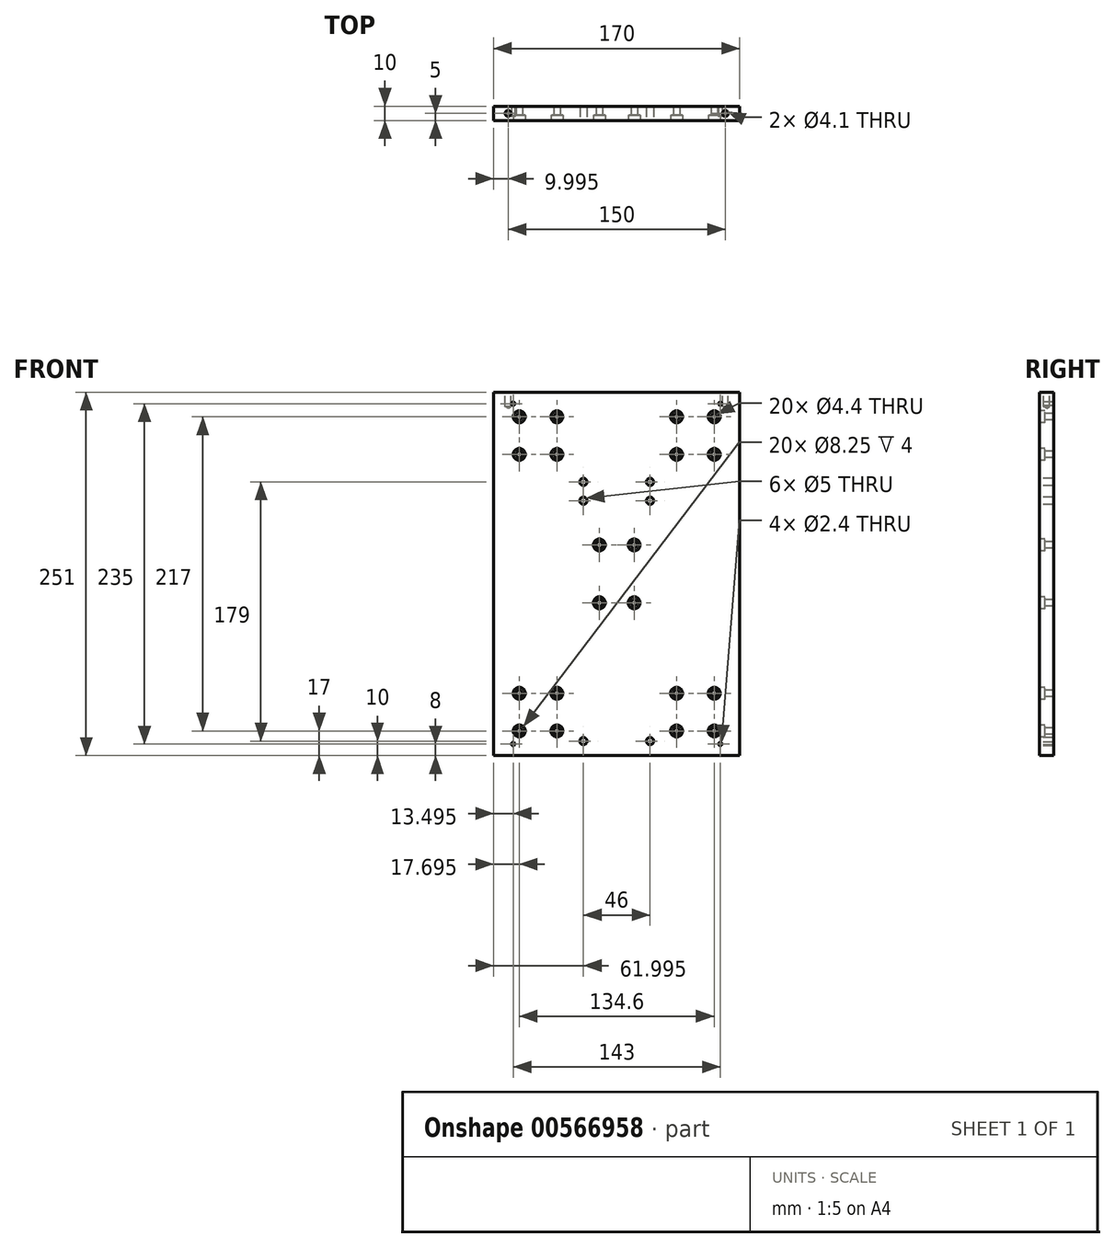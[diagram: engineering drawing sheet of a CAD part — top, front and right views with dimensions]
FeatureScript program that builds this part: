
annotation { "Feature Type Name" : "Feature", "Feature Type Description" : "" }
export const myFeature = defineFeature(function(context is Context, id is Id, definition is map)
    precondition{}
    {
        {
            var Q0;
            Q0=qCreatedBy(makeId("Front.planeOp"),FACE);
            var sketch = newSketch(context, id + "F0", { "sketchPlane" : qUnion([Q0])});
            skLineSegment(sketch, "E0.bottom", {"start": v(-43.58, 205.06) * mm, "end": v(126.42, 205.06) * mm});
            skLineSegment(sketch, "E0.top", {"start": v(-43.58, -40.94) * mm, "end": v(126.42, -40.94) * mm});
            skLineSegment(sketch, "E0.left", {"start": v(-43.58, 205.06) * mm, "end": v(-43.58, -40.94) * mm});
            skLineSegment(sketch, "E0.right", {"start": v(126.42, 205.06) * mm, "end": v(126.42, -40.94) * mm});
            skSolve(sketch);
        }
        {
            var Q0;
            Q0=makeQuery(id+"F0.imprint","IMPRINT",FACE,{"disambiguationData":[TD([[makeQuery(id+"F0.imprint","IMPRINT",EDGE,{"derivedFrom":sQuery(id+"F0.wireOp",EDGE,"E0.bottom")}),-1.0]])]});
            extrude(context, id + "F1", {"entities" : qUnion([Q0]), "depth" : 10 * mm});
        }
        {
            var Q0;
            Q0=makeQuery(id+"F1.opExtrude","CAP_FACE",FACE,{"disambiguationData":[OSD([sQuery(id+"F0.wireOp",EDGE,"E0.bottom"),sQuery(id+"F0.wireOp",EDGE,"E0.top"),sQuery(id+"F0.wireOp",EDGE,"E0.left"),sQuery(id+"F0.wireOp",EDGE,"E0.right")])],"isStart":false});
            var sketch = newSketch(context, id + "F2", { "sketchPlane" : qUnion([Q0])});
            skLineSegment(sketch, "E1", {"start": v(41.42, 205.06) * mm, "end": v(41.42, -40.94) * mm, "construction": true});
            skLineSegment(sketch, "E2", {"start": v(-30.08, 205.06) * mm, "end": v(-30.08, -40.94) * mm, "construction": true});
            skLineSegment(sketch, "E3.MirrorCS", {"start": v(112.92, 205.06) * mm, "end": v(112.92, -40.94) * mm, "construction": true});
            skLineSegment(sketch, "E4", {"start": v(112.92, 202.06) * mm, "end": v(-30.08, 202.06) * mm, "construction": true});
            skLineSegment(sketch, "E5", {"start": v(112.92, -32.94) * mm, "end": v(-30.08, -32.94) * mm, "construction": true});
            skPoint(sketch, "E6", {"position": v(112.92, 202.06) * mm});
            skPoint(sketch, "E7", {"position": v(-30.08, 202.06) * mm});
            skPoint(sketch, "E8", {"position": v(112.92, -32.94) * mm});
            skPoint(sketch, "E9", {"position": v(-30.08, -32.94) * mm});
            skPoint(sketch, "E10", {"position": v(18.42, -30.94) * mm});
            skPoint(sketch, "E11.MirrorP", {"position": v(64.42, -30.94) * mm});
            skLineSegment(sketch, "E12", {"start": v(112.92, 148.06) * mm, "end": v(-30.08, 148.06) * mm, "construction": true});
            skLineSegment(sketch, "E13", {"start": v(112.92, 135.06) * mm, "end": v(-30.08, 135.06) * mm, "construction": true});
            skPoint(sketch, "E14", {"position": v(64.42, 148.06) * mm});
            skPoint(sketch, "E15.MirrorP", {"position": v(18.42, 148.06) * mm});
            skPoint(sketch, "E16", {"position": v(64.42, 135.06) * mm});
            skPoint(sketch, "E17.MirrorP", {"position": v(18.42, 135.06) * mm});
            skLineSegment(sketch, "E18", {"start": v(41.42, 219.06) * mm, "end": v(11.42, 219.06) * mm, "construction": true});
            skLineSegment(sketch, "E19", {"start": v(11.42, 219.06) * mm, "end": v(11.42, 244.06) * mm, "construction": true});
            skLineSegment(sketch, "E20", {"start": v(11.42, 244.06) * mm, "end": v(41.42, 244.06) * mm, "construction": true});
            skLineSegment(sketch, "E21", {"start": v(-43.58, -10.94) * mm, "end": v(126.42, -10.94) * mm, "construction": true});
            skLineSegment(sketch, "E22", {"start": v(-43.58, 180.06) * mm, "end": v(126.42, 180.06) * mm, "construction": true});
            skPoint(sketch, "E23", {"position": v(-25.88, 2.06) * mm});
            skPoint(sketch, "E24.MirrorP", {"position": v(-25.88, -23.94) * mm});
            skPoint(sketch, "E25.MirrorP", {"position": v(108.72, 2.06) * mm});
            skPoint(sketch, "E26.MirrorP", {"position": v(108.72, -23.94) * mm});
            skPoint(sketch, "E27", {"position": v(0.12, 2.06) * mm});
            skPoint(sketch, "E28.MirrorP", {"position": v(82.72, 2.06) * mm});
            skPoint(sketch, "E29.MirrorP", {"position": v(0.12, -23.94) * mm});
            skPoint(sketch, "E30.MirrorP", {"position": v(82.72, -23.94) * mm});
            skPoint(sketch, "E31", {"position": v(-25.88, 193.06) * mm});
            skPoint(sketch, "E32.MirrorP", {"position": v(108.72, 193.06) * mm});
            skLineSegment(sketch, "E33", {"start": v(-25.88, 193.06) * mm, "end": v(108.72, 193.06) * mm, "construction": true});
            skPoint(sketch, "E34", {"position": v(0.12, 193.06) * mm});
            skPoint(sketch, "E35.MirrorP", {"position": v(82.72, 193.06) * mm});
            skPoint(sketch, "E36.MirrorP", {"position": v(-25.88, 167.06) * mm});
            skPoint(sketch, "E37.MirrorP", {"position": v(0.12, 167.06) * mm});
            skPoint(sketch, "E38.MirrorP", {"position": v(82.72, 167.06) * mm});
            skPoint(sketch, "E39.MirrorP", {"position": v(108.72, 167.06) * mm});
            skLineSegment(sketch, "E40", {"start": v(-10.35, 84.56) * mm, "end": v(93.03, 84.56) * mm, "construction": true});
            skPoint(sketch, "E41", {"position": v(29.42, 104.56) * mm});
            skPoint(sketch, "E42.MirrorP", {"position": v(53.42, 104.56) * mm});
            skPoint(sketch, "E43.MirrorP", {"position": v(53.42, 64.56) * mm});
            skPoint(sketch, "E44.MirrorP", {"position": v(29.42, 64.56) * mm});
            skSolve(sketch);
        }
        {
            var Q0;
            Q0=sQuery(id+"F2.wireOp",VERTEX,"E6");
            var Q1;
            Q1=sQuery(id+"F2.wireOp",VERTEX,"E7");
            var Q2;
            Q2=sQuery(id+"F2.wireOp",VERTEX,"E9");
            var Q3;
            Q3=sQuery(id+"F2.wireOp",VERTEX,"E8");
            var Q4;
            Q4=makeQuery(id+"F1.opExtrude","SWEPT_BODY",BODY,{"disambiguationData":[OSD([sQuery(id+"F0.wireOp",EDGE,"E0.bottom"),sQuery(id+"F0.wireOp",EDGE,"E0.top"),sQuery(id+"F0.wireOp",EDGE,"E0.left"),sQuery(id+"F0.wireOp",EDGE,"E0.right")])]});
            hole(context, id + "F3", {"style" : HoleStyle.SIMPLE, "endStyle" : HoleEndStyle.THROUGH, "standardTappedOrClearance" : lookupTablePath({ "standard" : "ISO", "engagement" : "75%", "pitch" : "0.6 mm", "size" : "M3", "type" : "Tapped" }), "standardBlindInLast" : lookupTablePath({ "standard" : "ISO", "engagement" : "75%", "pitch" : "0.6 mm", "size" : "M3", "type" : "Tapped" }), "holeDiameter" : 2.4 * mm, "locations" : qUnion([Q0, Q1, Q2, Q3]), "scope" : qUnion([Q4]), "tappedDepth" : 12 * mm, "tapClearance" : 3});
        }
        {
            var Q0;
            Q0=sQuery(id+"F2.wireOp",VERTEX,"E15.MirrorP");
            var Q1;
            Q1=sQuery(id+"F2.wireOp",VERTEX,"E14");
            var Q2;
            Q2=sQuery(id+"F2.wireOp",VERTEX,"E16");
            var Q3;
            Q3=sQuery(id+"F2.wireOp",VERTEX,"E17.MirrorP");
            var Q4;
            Q4=sQuery(id+"F2.wireOp",VERTEX,"E10");
            var Q5;
            Q5=sQuery(id+"F2.wireOp",VERTEX,"E11.MirrorP");
            var Q6;
            Q6=makeQuery(id+"F1.opExtrude","SWEPT_BODY",BODY,{"disambiguationData":[OSD([sQuery(id+"F0.wireOp",EDGE,"E0.bottom"),sQuery(id+"F0.wireOp",EDGE,"E0.top"),sQuery(id+"F0.wireOp",EDGE,"E0.left"),sQuery(id+"F0.wireOp",EDGE,"E0.right")])]});
            hole(context, id + "F4", {"style" : HoleStyle.SIMPLE, "endStyle" : HoleEndStyle.THROUGH, "standardTappedOrClearance" : lookupTablePath({ "standard" : "ISO", "engagement" : "75%", "pitch" : "1 mm", "size" : "M6", "type" : "Tapped" }), "standardBlindInLast" : lookupTablePath({ "standard" : "ISO", "engagement" : "75%", "pitch" : "1 mm", "size" : "M6", "type" : "Tapped" }), "holeDiameter" : 5 * mm, "locations" : qUnion([Q0, Q1, Q2, Q3, Q4, Q5]), "scope" : qUnion([Q6]), "isTappedThrough" : true, "majorDiameter" : 6 * mm, "showTappedDepth" : true});
        }
        {
            var Q0;
            Q0=makeQuery(id+"F1.opExtrude","SWEPT_FACE",FACE,{"disambiguationData":[OSD([sQuery(id+"F0.wireOp",EDGE,"E0.bottom")])]});
            extrude(context, id + "F5", {"entities" : qUnion([Q0]), "operationType" : NewBodyOperationType.ADD, "depth" : 5 * mm});
        }
        {
            var Q0;
            Q0=sQuery(id+"F2.wireOp",VERTEX,"E24.MirrorP");
            var Q1;
            Q1=sQuery(id+"F2.wireOp",VERTEX,"E23");
            var Q2;
            Q2=sQuery(id+"F2.wireOp",VERTEX,"E27");
            var Q3;
            Q3=sQuery(id+"F2.wireOp",VERTEX,"E29.MirrorP");
            var Q4;
            Q4=sQuery(id+"F2.wireOp",VERTEX,"E30.MirrorP");
            var Q5;
            Q5=sQuery(id+"F2.wireOp",VERTEX,"E28.MirrorP");
            var Q6;
            Q6=sQuery(id+"F2.wireOp",VERTEX,"E25.MirrorP");
            var Q7;
            Q7=sQuery(id+"F2.wireOp",VERTEX,"E26.MirrorP");
            var Q8;
            Q8=sQuery(id+"F2.wireOp",VERTEX,"E31");
            var Q9;
            Q9=sQuery(id+"F2.wireOp",VERTEX,"E36.MirrorP");
            var Q10;
            Q10=sQuery(id+"F2.wireOp",VERTEX,"E37.MirrorP");
            var Q11;
            Q11=sQuery(id+"F2.wireOp",VERTEX,"E34");
            var Q12;
            Q12=sQuery(id+"F2.wireOp",VERTEX,"E35.MirrorP");
            var Q13;
            Q13=sQuery(id+"F2.wireOp",VERTEX,"E32.MirrorP");
            var Q14;
            Q14=sQuery(id+"F2.wireOp",VERTEX,"E39.MirrorP");
            var Q15;
            Q15=sQuery(id+"F2.wireOp",VERTEX,"E38.MirrorP");
            var Q16;
            Q16=makeQuery(id+"F1.opExtrude","SWEPT_BODY",BODY,{"disambiguationData":[OSD([sQuery(id+"F0.wireOp",EDGE,"E0.bottom"),sQuery(id+"F0.wireOp",EDGE,"E0.top"),sQuery(id+"F0.wireOp",EDGE,"E0.left"),sQuery(id+"F0.wireOp",EDGE,"E0.right")])]});
            hole(context, id + "F6", {"style" : HoleStyle.C_BORE, "endStyle" : HoleEndStyle.THROUGH, "standardTappedOrClearance" : lookupTablePath({ "standard" : "ISO", "fit" : "Normal", "size" : "M4", "type" : "Clearance" }), "standardBlindInLast" : lookupTablePath({ "fit" : "Standard", "standard" : "ISO", "size" : "M4", "type" : "Clearance" }), "holeDiameter" : 4.4 * mm, "cBoreDiameter" : 8.25 * mm, "cBoreDepth" : 4 * mm, "locations" : qUnion([Q0, Q1, Q2, Q3, Q4, Q5, Q6, Q7, Q8, Q9, Q10, Q11, Q12, Q13, Q14, Q15]), "scope" : qUnion([Q16]), "isTappedThrough" : true});
        }
        {
            var Q0;
            Q0=makeQuery(id+"F5.opExtrude","CAP_FACE",FACE,{"disambiguationData":[OSD([sQuery(id+"F0.wireOp",EDGE,"E0.bottom")])],"isStart":false});
            var sketch = newSketch(context, id + "F7", { "sketchPlane" : qUnion([Q0])});
            skLineSegment(sketch, "E45", {"start": v(126.42, -5) * mm, "end": v(-43.58, -5) * mm, "construction": true});
            skPoint(sketch, "E46", {"position": v(116.42, -5) * mm});
            skPoint(sketch, "E47", {"position": v(-33.58, -5) * mm});
            skSolve(sketch);
        }
        {
            var Q0;
            Q0=sQuery(id+"F7.wireOp",VERTEX,"E47");
            var Q1;
            Q1=sQuery(id+"F7.wireOp",VERTEX,"E46");
            var Q2;
            Q2=makeQuery(id+"F1.opExtrude","SWEPT_BODY",BODY,{"disambiguationData":[OSD([sQuery(id+"F0.wireOp",EDGE,"E0.bottom"),sQuery(id+"F0.wireOp",EDGE,"E0.top"),sQuery(id+"F0.wireOp",EDGE,"E0.left"),sQuery(id+"F0.wireOp",EDGE,"E0.right")])]});
            hole(context, id + "F8", {"style" : HoleStyle.SIMPLE, "endStyle" : HoleEndStyle.BLIND, "standardTappedOrClearance" : lookupTablePath({ "standard" : "ISO", "engagement" : "75%", "pitch" : "0.9 mm", "size" : "M5", "type" : "Tapped" }), "standardBlindInLast" : lookupTablePath({ "standard" : "ISO", "engagement" : "75%", "pitch" : "0.9 mm", "size" : "M5", "type" : "Tapped" }), "holeDiameter" : 4.1 * mm, "holeDepth" : 10 * mm, "locations" : qUnion([Q0, Q1]), "scope" : qUnion([Q2])});
        }
        {
            var Q0;
            Q0=sQuery(id+"F2.wireOp",VERTEX,"E41");
            var Q1;
            Q1=sQuery(id+"F2.wireOp",VERTEX,"E42.MirrorP");
            var Q2;
            Q2=sQuery(id+"F2.wireOp",VERTEX,"E43.MirrorP");
            var Q3;
            Q3=sQuery(id+"F2.wireOp",VERTEX,"E44.MirrorP");
            var Q4;
            Q4=makeQuery(id+"F1.opExtrude","SWEPT_BODY",BODY,{"disambiguationData":[OSD([sQuery(id+"F0.wireOp",EDGE,"E0.bottom"),sQuery(id+"F0.wireOp",EDGE,"E0.top"),sQuery(id+"F0.wireOp",EDGE,"E0.left"),sQuery(id+"F0.wireOp",EDGE,"E0.right")])]});
            hole(context, id + "F9", {"style" : HoleStyle.C_BORE, "endStyle" : HoleEndStyle.THROUGH, "standardTappedOrClearance" : lookupTablePath({ "standard" : "ISO", "fit" : "Normal", "size" : "M4", "type" : "Clearance" }), "standardBlindInLast" : lookupTablePath({ "fit" : "Standard", "standard" : "ISO", "size" : "M4", "type" : "Clearance" }), "holeDiameter" : 4.4 * mm, "cBoreDiameter" : 8.25 * mm, "cBoreDepth" : 4 * mm, "locations" : qUnion([Q0, Q1, Q2, Q3]), "scope" : qUnion([Q4]), "isTappedThrough" : true});
        }
    });
